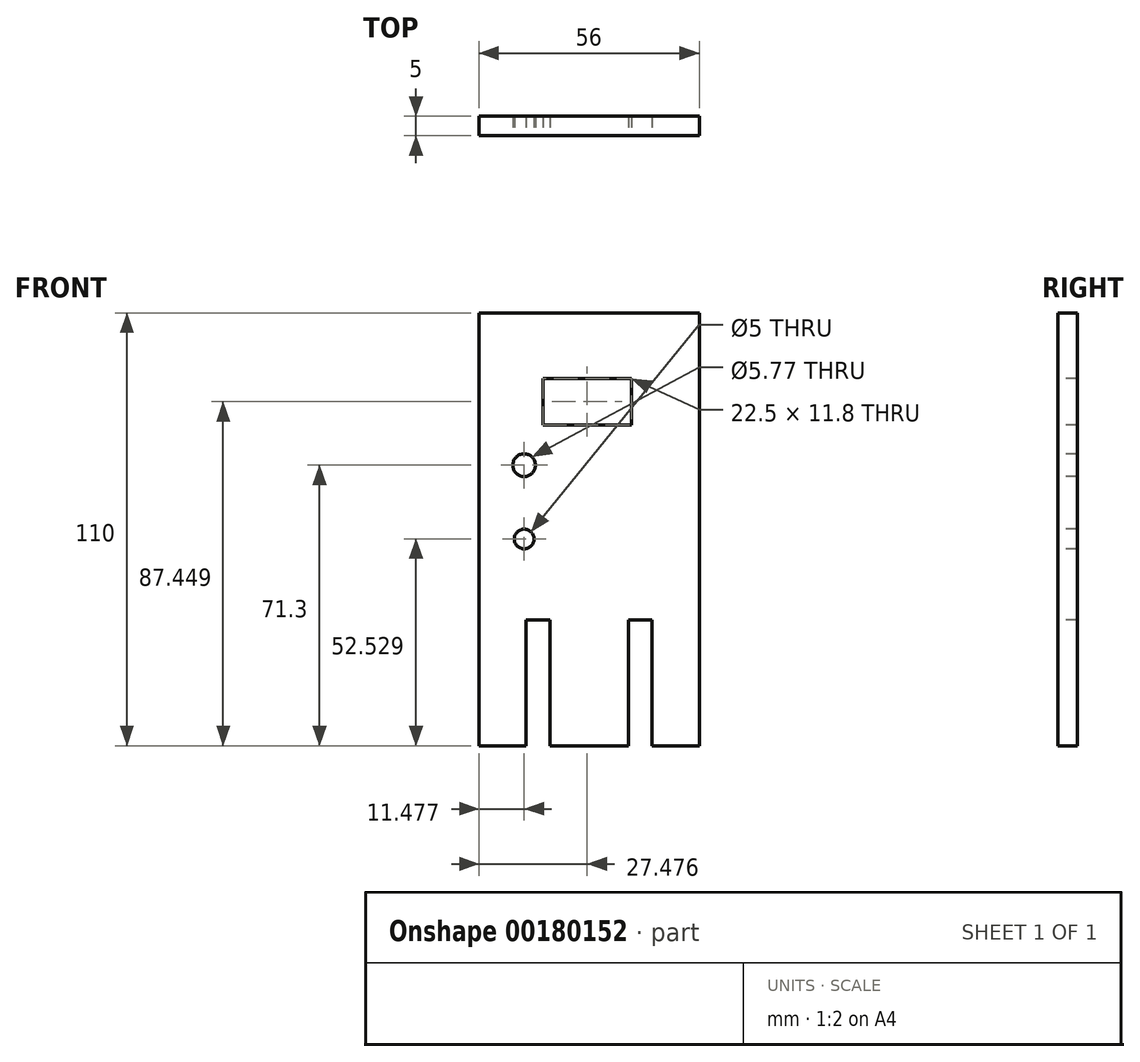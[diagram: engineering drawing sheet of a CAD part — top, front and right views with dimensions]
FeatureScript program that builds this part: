
annotation { "Feature Type Name" : "Feature", "Feature Type Description" : "" }
export const myFeature = defineFeature(function(context is Context, id is Id, definition is map)
    precondition{}
    {
        {
            var Q0;
            Q0=qCreatedBy(makeId("Front.planeOp"),FACE);
            var sketch = newSketch(context, id + "F0", { "sketchPlane" : qUnion([Q0])});
            skLineSegment(sketch, "E0", {"start": v(12.23, 67.6) * mm, "end": v(-43.77, 67.6) * mm});
            skLineSegment(sketch, "E1", {"start": v(-43.77, 67.6) * mm, "end": v(-43.77, -42.4) * mm});
            skLineSegment(sketch, "E2", {"start": v(-43.77, -42.4) * mm, "end": v(12.23, -42.4) * mm});
            skLineSegment(sketch, "E3", {"start": v(12.23, -42.4) * mm, "end": v(12.23, 67.6) * mm});
            skSolve(sketch);
        }
        {
            var Q0;
            Q0 = qSketchRegion(id + "F0", true);
            extrude(context, id + "F1", {"entities" : qUnion([Q0]), "depth" : 5 * mm});
        }
        {
            var Q0;
            Q0=makeQuery(id+"F1.opExtrude","CAP_FACE",FACE,{"disambiguationData":[OSD([sQuery(id+"F0.wireOp",EDGE,"E0"),sQuery(id+"F0.wireOp",EDGE,"E1"),sQuery(id+"F0.wireOp",EDGE,"E2"),sQuery(id+"F0.wireOp",EDGE,"E3")])],"isStart":false});
            var sketch = newSketch(context, id + "F2", { "sketchPlane" : qUnion([Q0])});
            skLineSegment(sketch, "E4", {"start": v(-5.77, -42.4) * mm, "end": v(-5.77, -10.4) * mm});
            skLineSegment(sketch, "E5", {"start": v(-5.77, -10.4) * mm, "end": v(0.23, -10.4) * mm});
            skLineSegment(sketch, "E6", {"start": v(0.23, -10.4) * mm, "end": v(0.23, -42.4) * mm});
            skLineSegment(sketch, "E7", {"start": v(0.23, -42.4) * mm, "end": v(-5.77, -42.4) * mm});
            skLineSegment(sketch, "E8", {"start": v(-25.77, -42.4) * mm, "end": v(-25.77, -10.4) * mm});
            skLineSegment(sketch, "E9", {"start": v(-25.77, -10.4) * mm, "end": v(-31.77, -10.4) * mm});
            skLineSegment(sketch, "E10", {"start": v(-31.77, -10.4) * mm, "end": v(-31.77, -42.4) * mm});
            skLineSegment(sketch, "E11", {"start": v(-31.77, -42.4) * mm, "end": v(-25.77, -42.4) * mm});
            skLineSegment(sketch, "E12", {"start": v(-5.04, 50.94) * mm, "end": v(-27.54, 50.94) * mm});
            skLineSegment(sketch, "E13", {"start": v(-27.54, 50.94) * mm, "end": v(-27.54, 39.14) * mm});
            skLineSegment(sketch, "E14", {"start": v(-27.54, 39.14) * mm, "end": v(-5.04, 39.14) * mm});
            skLineSegment(sketch, "E15", {"start": v(-5.04, 39.14) * mm, "end": v(-5.04, 50.94) * mm});
            skCircle(sketch, "E16", {"center": v(-32.3, 28.89) * mm, "radius": 2.88 * mm});
            skCircle(sketch, "E17", {"center": v(-32.3, 10.12) * mm, "radius": 2.5 * mm});
            skSolve(sketch);
        }
        {
            var Q0;
            Q0 = qSketchRegion(id + "F2", true);
            extrude(context, id + "F3", {"entities" : qUnion([Q0]), "operationType" : NewBodyOperationType.REMOVE, "oppositeDirection" : true, "depth" : 25 * mm});
        }
    });
